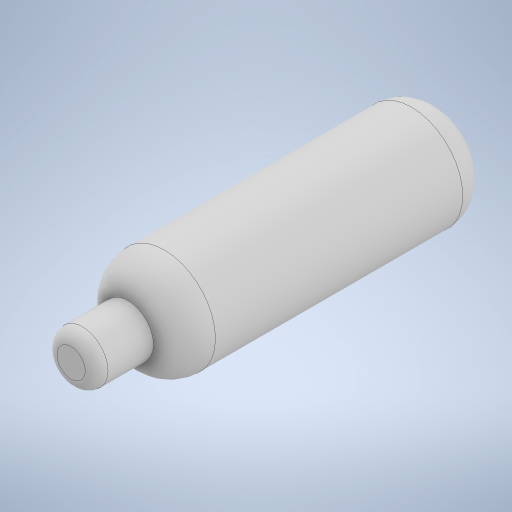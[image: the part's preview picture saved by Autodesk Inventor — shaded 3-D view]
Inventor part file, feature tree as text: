
AUTODESK INVENTOR PART (.ipt)
format: ipt  version: 2023 (Build 270158000, 158)  size: 248,320 bytes
history: native  units: in
note: dims shown in document units (in); Inventor stores cm internally (conversion verified against a paired STEP export)
features: fillet x3, extrude x2, sketch x2
ambient origin geometry x8: Origin, YZ Plane, XZ Plane, XY Plane, X Axis, Y Axis, Z Axis, Center Point
bodies: Solid1 (feature_tree)
feature tree (7):
  extrude  "Extrusion1"  Depth=0.3543in
  extrude  "Extrusion2"  Depth=0.3543in
  fillet  "Fillet1"  Radius=0.3937in
  fillet  "Fillet2"  Radius=0.2662in
  fillet  "Fillet3"  Radius=0.0787in
  sketch  "Sketch1"  dims[d0=0.7087in d1=0.3543in]
  sketch  "Sketch2"  dims[d2=2.1654in d3=0.0in d4=0.3543in d5=0.3937in d6=0.0in d7=0.2662in d8=0.0787in d9=0.2037in]
